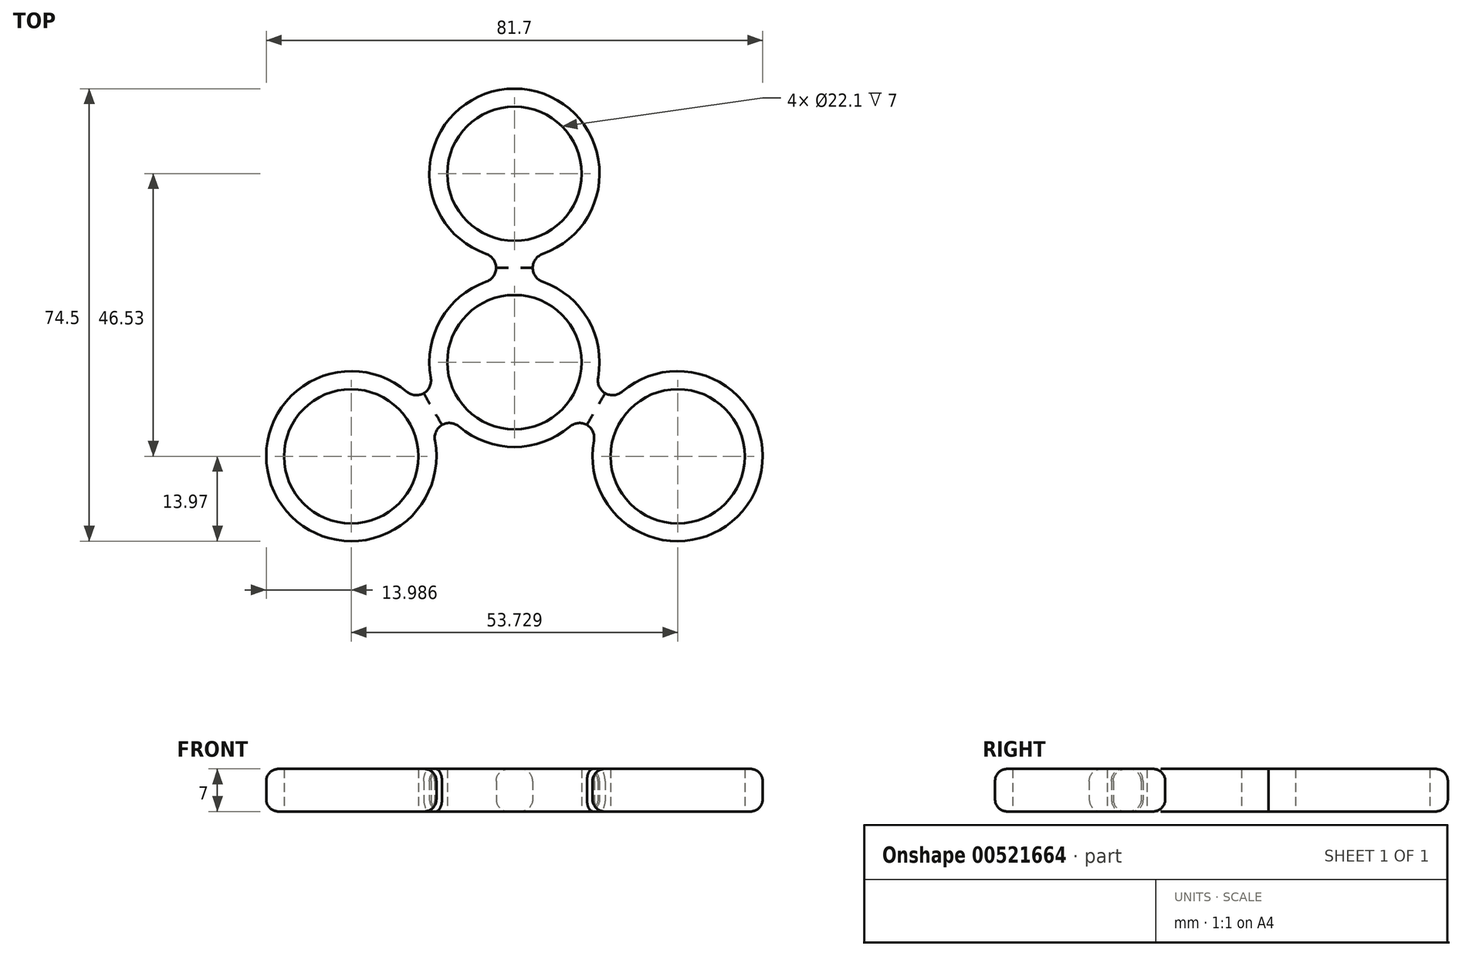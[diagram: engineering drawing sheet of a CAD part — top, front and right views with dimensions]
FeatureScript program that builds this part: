
annotation { "Feature Type Name" : "Feature", "Feature Type Description" : "" }
export const myFeature = defineFeature(function(context is Context, id is Id, definition is map)
    precondition{}
    {
        {
            var Q0;
            Q0=qCreatedBy(makeId("Top.planeOp"),FACE);
            var sketch = newSketch(context, id + "F0", { "sketchPlane" : qUnion([Q0])});
            skCircle(sketch, "E0", {"center": v(0, 31) * mm, "radius": 11.05 * mm});
            skCircle(sketch, "E1.1.0", {"center": v(-26.86, -15.53) * mm, "radius": 11.05 * mm});
            skCircle(sketch, "E1.2.0", {"center": v(26.86, -15.53) * mm, "radius": 11.05 * mm});
            skPoint(sketch, "E1.center", {"position": v(0, -0.02) * mm});
            skCircle(sketch, "E2", {"center": v(0, 31) * mm, "radius": 14 * mm});
            skCircle(sketch, "E3.1.0", {"center": v(-26.85, -15.5) * mm, "radius": 14 * mm});
            skCircle(sketch, "E3.2.0", {"center": v(26.85, -15.5) * mm, "radius": 14 * mm});
            skPoint(sketch, "E3.center", {"position": v(0, 0) * mm});
            skCircle(sketch, "E4", {"center": v(0, -0.02) * mm, "radius": 11.05 * mm});
            skCircle(sketch, "E5", {"center": v(0, 0) * mm, "radius": 14 * mm});
            skLineSegment(sketch, "E6", {"start": v(-26.86, -15.53) * mm, "end": v(0, -0.02) * mm, "construction": true});
            skLineSegment(sketch, "E7.bottom", {"start": v(3, 18.98) * mm, "end": v(-3, 18.98) * mm});
            skLineSegment(sketch, "E7.top", {"start": v(3, 11.98) * mm, "end": v(-3, 11.98) * mm});
            skLineSegment(sketch, "E7.left", {"start": v(3, 18.98) * mm, "end": v(3, 11.98) * mm});
            skLineSegment(sketch, "E7.right", {"start": v(-3, 18.98) * mm, "end": v(-3, 11.98) * mm});
            skPoint(sketch, "E7.middle", {"position": v(0, 15.48) * mm});
            skLineSegment(sketch, "E8.1.0", {"start": v(-17.94, -6.9) * mm, "end": v(-11.87, -3.4) * mm});
            skLineSegment(sketch, "E8.1.1", {"start": v(-14.94, -12.09) * mm, "end": v(-8.87, -8.59) * mm});
            skLineSegment(sketch, "E8.1.2", {"start": v(-17.94, -6.9) * mm, "end": v(-14.94, -12.09) * mm});
            skLineSegment(sketch, "E8.1.3", {"start": v(-11.87, -3.4) * mm, "end": v(-8.87, -8.59) * mm});
            skLineSegment(sketch, "E8.2.0", {"start": v(14.94, -12.09) * mm, "end": v(8.87, -8.59) * mm});
            skLineSegment(sketch, "E8.2.1", {"start": v(17.94, -6.9) * mm, "end": v(11.87, -3.4) * mm});
            skLineSegment(sketch, "E8.2.2", {"start": v(14.94, -12.09) * mm, "end": v(17.94, -6.9) * mm});
            skLineSegment(sketch, "E8.2.3", {"start": v(8.87, -8.59) * mm, "end": v(11.87, -3.4) * mm});
            skSolve(sketch);
        }
        {
            var Q0;
            Q0=makeQuery(id+"F0.imprint","IMPRINT",FACE,{"disambiguationData":[TD([[makeQuery(id+"F0.imprint","IMPRINT",EDGE,{"derivedFrom":sQuery(id+"F0.wireOp",EDGE,"E1.1.0")}),-1.0]])]});
            var Q1;
            {var subQ5=sQuery(id+"F0.wireOp",EDGE,"E8.1.2");Q1=makeQuery(id+"F0.imprint","IMPRINT",FACE,{"disambiguationData":[TD([[makeQuery(id+"F0.imprint","IMPRINT",EDGE,{"derivedFrom":subQ5}),1.0]])]});}
            var Q2;
            {var subQ0=sQuery(id+"F0.wireOp",EDGE,"E8.1.0");var subQ1=sQuery(id+"F0.wireOp",EDGE,"E3.1.0");var subQ2=makeQuery(id+"F0.imprint","INTERSECT",VERTEX,{"derivedFrom":[subQ1,subQ0]});Q2=makeQuery(id+"F0.imprint","IMPRINT",FACE,{"disambiguationData":[TD([[makeQuery(id+"F0.imprint","IMPRINT",EDGE,{"disambiguationData":[TD([[subQ2,1.0]])],"derivedFrom":subQ1}),-1.0]])]});}
            var Q3;
            {var subQ5=sQuery(id+"F0.wireOp",EDGE,"E8.1.3");Q3=makeQuery(id+"F0.imprint","IMPRINT",FACE,{"disambiguationData":[TD([[makeQuery(id+"F0.imprint","IMPRINT",EDGE,{"derivedFrom":subQ5}),-1.0]])]});}
            var Q4;
            Q4=makeQuery(id+"F0.imprint","IMPRINT",FACE,{"disambiguationData":[TD([[makeQuery(id+"F0.imprint","IMPRINT",EDGE,{"derivedFrom":sQuery(id+"F0.wireOp",EDGE,"E4")}),-1.0]])]});
            var Q5;
            {var subQ5=sQuery(id+"F0.wireOp",EDGE,"E8.2.3");Q5=makeQuery(id+"F0.imprint","IMPRINT",FACE,{"disambiguationData":[TD([[makeQuery(id+"F0.imprint","IMPRINT",EDGE,{"derivedFrom":subQ5}),-1.0]])]});}
            var Q6;
            {var subQ0=sQuery(id+"F0.wireOp",EDGE,"E8.2.0");var subQ1=sQuery(id+"F0.wireOp",EDGE,"E3.2.0");var subQ2=makeQuery(id+"F0.imprint","INTERSECT",VERTEX,{"derivedFrom":[subQ1,subQ0]});Q6=makeQuery(id+"F0.imprint","IMPRINT",FACE,{"disambiguationData":[TD([[makeQuery(id+"F0.imprint","IMPRINT",EDGE,{"disambiguationData":[TD([[subQ2,1.0]])],"derivedFrom":subQ1}),-1.0]])]});}
            var Q7;
            {var subQ5=sQuery(id+"F0.wireOp",EDGE,"E8.2.2");Q7=makeQuery(id+"F0.imprint","IMPRINT",FACE,{"disambiguationData":[TD([[makeQuery(id+"F0.imprint","IMPRINT",EDGE,{"derivedFrom":subQ5}),1.0]])]});}
            var Q8;
            Q8=makeQuery(id+"F0.imprint","IMPRINT",FACE,{"disambiguationData":[TD([[makeQuery(id+"F0.imprint","IMPRINT",EDGE,{"derivedFrom":sQuery(id+"F0.wireOp",EDGE,"E1.2.0")}),-1.0]])]});
            var Q9;
            {var subQ5=sQuery(id+"F0.wireOp",EDGE,"E7.top");Q9=makeQuery(id+"F0.imprint","IMPRINT",FACE,{"disambiguationData":[TD([[makeQuery(id+"F0.imprint","IMPRINT",EDGE,{"derivedFrom":subQ5}),-1.0]])]});}
            var Q10;
            {var subQ0=sQuery(id+"F0.wireOp",EDGE,"E7.left");var subQ1=sQuery(id+"F0.wireOp",EDGE,"E2");var subQ2=makeQuery(id+"F0.imprint","INTERSECT",VERTEX,{"derivedFrom":[subQ1,subQ0]});Q10=makeQuery(id+"F0.imprint","IMPRINT",FACE,{"disambiguationData":[TD([[makeQuery(id+"F0.imprint","IMPRINT",EDGE,{"disambiguationData":[TD([[subQ2,1.0]])],"derivedFrom":subQ1}),-1.0]])]});}
            var Q11;
            {var subQ5=sQuery(id+"F0.wireOp",EDGE,"E7.bottom");Q11=makeQuery(id+"F0.imprint","IMPRINT",FACE,{"disambiguationData":[TD([[makeQuery(id+"F0.imprint","IMPRINT",EDGE,{"derivedFrom":subQ5}),1.0]])]});}
            var Q12;
            Q12=makeQuery(id+"F0.imprint","IMPRINT",FACE,{"disambiguationData":[TD([[makeQuery(id+"F0.imprint","IMPRINT",EDGE,{"derivedFrom":sQuery(id+"F0.wireOp",EDGE,"E0")}),-1.0]])]});
            extrude(context, id + "F1", {"entities" : qUnion([Q0, Q1, Q2, Q3, Q4, Q5, Q6, Q7, Q8, Q9, Q10, Q11, Q12]), "depth" : 7 * mm, "offsetDistance" : 25 * mm});
        }
        {
            var Q0;
            Q0=makeQuery(id+"F1.opExtrude","SWEPT_EDGE",EDGE,{"disambiguationData":[OSD([sQuery(id+"F0.wireOp",EDGE,"E5"),sQuery(id+"F0.wireOp",EDGE,"E8.2.1")])]});
            var Q1;
            Q1=makeQuery(id+"F1.opExtrude","SWEPT_EDGE",EDGE,{"disambiguationData":[OSD([sQuery(id+"F0.wireOp",EDGE,"E5"),sQuery(id+"F0.wireOp",EDGE,"E7.left")])]});
            var Q2;
            Q2=makeQuery(id+"F1.opExtrude","SWEPT_EDGE",EDGE,{"disambiguationData":[OSD([sQuery(id+"F0.wireOp",EDGE,"E3.2.0"),sQuery(id+"F0.wireOp",EDGE,"E8.2.1")])]});
            var Q3;
            Q3=makeQuery(id+"F1.opExtrude","SWEPT_EDGE",EDGE,{"disambiguationData":[OSD([sQuery(id+"F0.wireOp",EDGE,"E2"),sQuery(id+"F0.wireOp",EDGE,"E7.left")])]});
            var Q4;
            Q4=makeQuery(id+"F1.opExtrude","SWEPT_EDGE",EDGE,{"disambiguationData":[OSD([sQuery(id+"F0.wireOp",EDGE,"E3.1.0"),sQuery(id+"F0.wireOp",EDGE,"E8.1.1")])]});
            var Q5;
            Q5=makeQuery(id+"F1.opExtrude","SWEPT_EDGE",EDGE,{"disambiguationData":[OSD([sQuery(id+"F0.wireOp",EDGE,"E5"),sQuery(id+"F0.wireOp",EDGE,"E8.1.1")])]});
            var Q6;
            Q6=makeQuery(id+"F1.opExtrude","SWEPT_EDGE",EDGE,{"disambiguationData":[OSD([sQuery(id+"F0.wireOp",EDGE,"E5"),sQuery(id+"F0.wireOp",EDGE,"E8.2.0")])]});
            var Q7;
            Q7=makeQuery(id+"F1.opExtrude","SWEPT_EDGE",EDGE,{"disambiguationData":[OSD([sQuery(id+"F0.wireOp",EDGE,"E3.2.0"),sQuery(id+"F0.wireOp",EDGE,"E8.2.0")])]});
            var Q8;
            Q8=makeQuery(id+"F1.opExtrude","SWEPT_EDGE",EDGE,{"disambiguationData":[OSD([sQuery(id+"F0.wireOp",EDGE,"E2"),sQuery(id+"F0.wireOp",EDGE,"E7.right")])]});
            var Q9;
            Q9=makeQuery(id+"F1.opExtrude","SWEPT_EDGE",EDGE,{"disambiguationData":[OSD([sQuery(id+"F0.wireOp",EDGE,"E5"),sQuery(id+"F0.wireOp",EDGE,"E7.right")])]});
            var Q10;
            Q10=makeQuery(id+"F1.opExtrude","SWEPT_EDGE",EDGE,{"disambiguationData":[OSD([sQuery(id+"F0.wireOp",EDGE,"E5"),sQuery(id+"F0.wireOp",EDGE,"E8.1.0")])]});
            var Q11;
            Q11=makeQuery(id+"F1.opExtrude","SWEPT_EDGE",EDGE,{"disambiguationData":[OSD([sQuery(id+"F0.wireOp",EDGE,"E3.1.0"),sQuery(id+"F0.wireOp",EDGE,"E8.1.0")])]});
            fillet(context, id + "F2", {"entities" : qUnion([Q0, Q1, Q2, Q3, Q4, Q5, Q6, Q7, Q8, Q9, Q10, Q11]), "radius" : 2.5 * mm, "tangentPropagation" : true, "allowEdgeOverflow" : false});
        }
        {
            var Q0;
            Q0=makeQuery(id+"F1.opExtrude","CAP_EDGE",EDGE,{"disambiguationData":[OSD([sQuery(id+"F0.wireOp",EDGE,"E3.2.0")])],"isStart":false});
            var Q1;
            Q1=makeQuery(id+"F1.opExtrude","CAP_EDGE",EDGE,{"disambiguationData":[OSD([sQuery(id+"F0.wireOp",EDGE,"E3.2.0")])],"isStart":true});
            var Q2;
            {var subQ0=sQuery(id+"F0.wireOp",EDGE,"E5");Q2=makeQuery(id+"F1.opExtrude","CAP_EDGE",EDGE,{"disambiguationData":[OSD([subQ0]),TDD([makeQuery(id+"F0.imprint","IMPRINT",EDGE,{"disambiguationData":[TD([[makeQuery(id+"F0.imprint","INTERSECT",VERTEX,{"derivedFrom":[subQ0,sQuery(id+"F0.wireOp",EDGE,"E7.left")]}),1.0]])],"derivedFrom":subQ0})])],"isStart":false});}
            var Q3;
            {var subQ0=sQuery(id+"F0.wireOp",EDGE,"E5");Q3=makeQuery(id+"F1.opExtrude","CAP_EDGE",EDGE,{"disambiguationData":[OSD([subQ0]),TDD([makeQuery(id+"F0.imprint","IMPRINT",EDGE,{"disambiguationData":[TD([[makeQuery(id+"F0.imprint","INTERSECT",VERTEX,{"derivedFrom":[subQ0,sQuery(id+"F0.wireOp",EDGE,"E7.left")]}),1.0]])],"derivedFrom":subQ0})])],"isStart":true});}
            var Q4;
            Q4=makeQuery(id+"F1.opExtrude","CAP_EDGE",EDGE,{"disambiguationData":[OSD([sQuery(id+"F0.wireOp",EDGE,"E2")])],"isStart":false});
            var Q5;
            Q5=makeQuery(id+"F1.opExtrude","CAP_EDGE",EDGE,{"disambiguationData":[OSD([sQuery(id+"F0.wireOp",EDGE,"E2")])],"isStart":true});
            var Q6;
            {var subQ0=sQuery(id+"F0.wireOp",EDGE,"E5");Q6=makeQuery(id+"F1.opExtrude","CAP_EDGE",EDGE,{"disambiguationData":[OSD([subQ0]),TDD([makeQuery(id+"F0.imprint","IMPRINT",EDGE,{"disambiguationData":[TD([[makeQuery(id+"F0.imprint","INTERSECT",VERTEX,{"derivedFrom":[subQ0,sQuery(id+"F0.wireOp",EDGE,"E7.right")]}),-1.0]])],"derivedFrom":subQ0})])],"isStart":false});}
            var Q7;
            Q7=makeQuery(id+"F1.opExtrude","CAP_EDGE",EDGE,{"disambiguationData":[OSD([sQuery(id+"F0.wireOp",EDGE,"E3.1.0")])],"isStart":true});
            var Q8;
            Q8=makeQuery(id+"F1.opExtrude","CAP_EDGE",EDGE,{"disambiguationData":[OSD([sQuery(id+"F0.wireOp",EDGE,"E3.1.0")])],"isStart":false});
            var Q9;
            {var subQ0=sQuery(id+"F0.wireOp",EDGE,"E5");Q9=makeQuery(id+"F1.opExtrude","CAP_EDGE",EDGE,{"disambiguationData":[OSD([subQ0]),TDD([makeQuery(id+"F0.imprint","IMPRINT",EDGE,{"disambiguationData":[TD([[makeQuery(id+"F0.imprint","INTERSECT",VERTEX,{"derivedFrom":[subQ0,sQuery(id+"F0.wireOp",EDGE,"E8.1.1")]}),-1.0]])],"derivedFrom":subQ0})])],"isStart":false});}
            var Q10;
            {var subQ0=sQuery(id+"F0.wireOp",EDGE,"E5");Q10=makeQuery(id+"F1.opExtrude","CAP_EDGE",EDGE,{"disambiguationData":[OSD([subQ0]),TDD([makeQuery(id+"F0.imprint","IMPRINT",EDGE,{"disambiguationData":[TD([[makeQuery(id+"F0.imprint","INTERSECT",VERTEX,{"derivedFrom":[subQ0,sQuery(id+"F0.wireOp",EDGE,"E8.1.1")]}),-1.0]])],"derivedFrom":subQ0})])],"isStart":true});}
            var Q11;
            {var subQ0=sQuery(id+"F0.wireOp",EDGE,"E5");Q11=makeQuery(id+"F1.opExtrude","CAP_EDGE",EDGE,{"disambiguationData":[OSD([subQ0]),TDD([makeQuery(id+"F0.imprint","IMPRINT",EDGE,{"disambiguationData":[TD([[makeQuery(id+"F0.imprint","INTERSECT",VERTEX,{"derivedFrom":[subQ0,sQuery(id+"F0.wireOp",EDGE,"E7.right")]}),-1.0]])],"derivedFrom":subQ0})])],"isStart":true});}
            fillet(context, id + "F3", {"entities" : qUnion([Q0, Q1, Q2, Q3, Q4, Q5, Q6, Q7, Q8, Q9, Q10, Q11]), "radius" : 2 * mm, "tangentPropagation" : true, "allowEdgeOverflow" : false});
        }
    });
